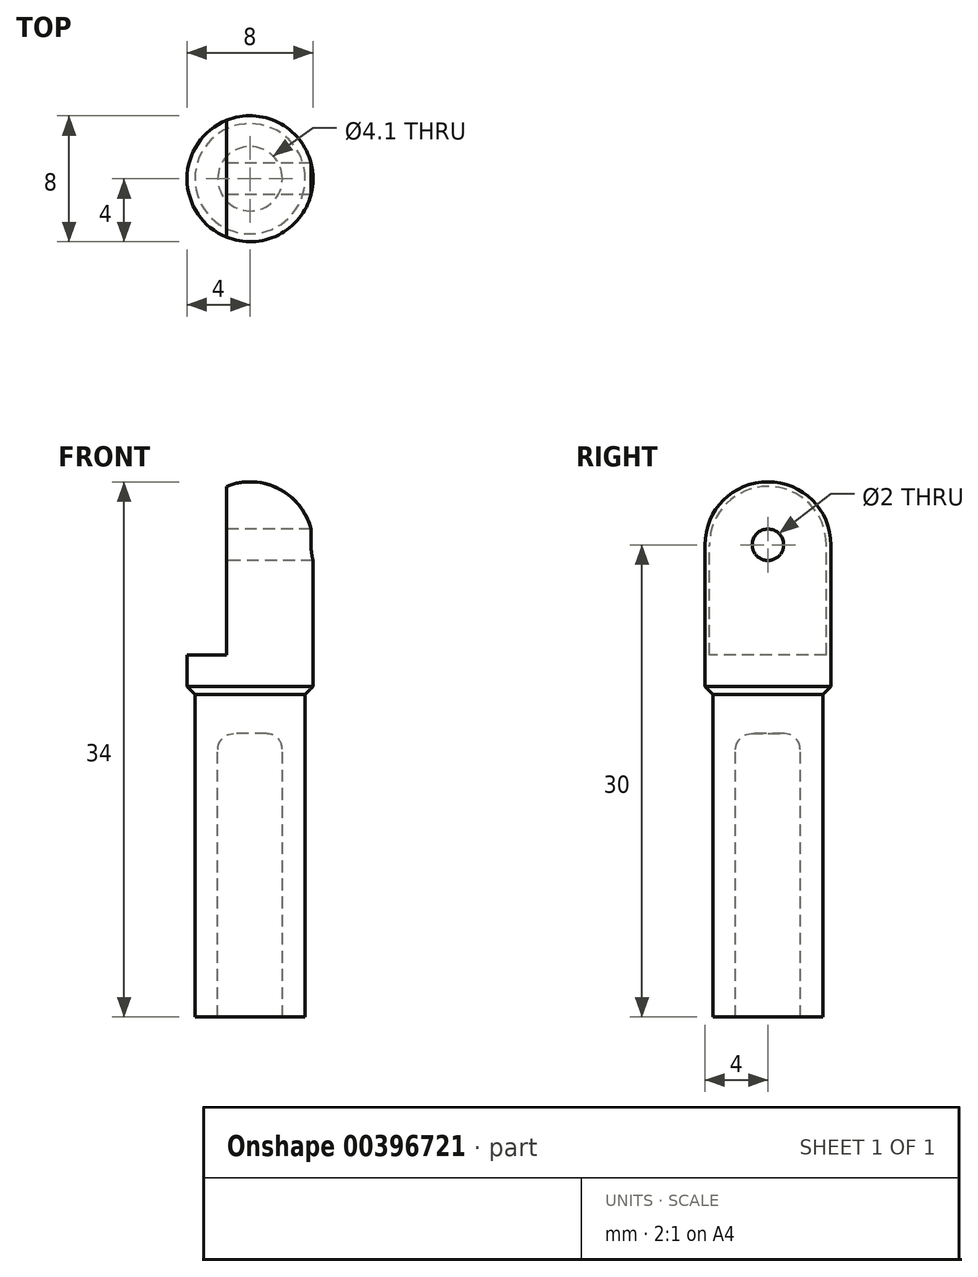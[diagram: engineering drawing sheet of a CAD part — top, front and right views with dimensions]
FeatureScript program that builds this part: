
annotation { "Feature Type Name" : "Feature", "Feature Type Description" : "" }
export const myFeature = defineFeature(function(context is Context, id is Id, definition is map)
    precondition{}
    {
        {
            var Q0;
            Q0=qCreatedBy(makeId("Front.planeOp"),FACE);
            var sketch = newSketch(context, id + "F0", { "sketchPlane" : qUnion([Q0])});
            skLineSegment(sketch, "E0", {"start": v(0, 16) * mm, "end": v(0, 0) * mm, "construction": true});
            skLineSegment(sketch, "E1", {"start": v(2.05, -18) * mm, "end": v(3.5, -18) * mm});
            skLineSegment(sketch, "E2", {"start": v(3.5, -18) * mm, "end": v(3.5, 2.5) * mm});
            skLineSegment(sketch, "E3", {"start": v(4, 3) * mm, "end": v(4, 12) * mm});
            skArc(sketch, "E4", {"start": v(4, 12) * mm, "mid": v(2.83, 14.83) * mm, "end": v(0, 16) * mm});
            skLineSegment(sketch, "E5", {"start": v(0, 16) * mm, "end": v(0, 12) * mm});
            skLineSegment(sketch, "E6", {"start": v(2.05, -18) * mm, "end": v(2.05, -1) * mm});
            skLineSegment(sketch, "E7", {"start": v(1.05, 0) * mm, "end": v(0, 0) * mm});
            skLineSegment(sketch, "E8", {"start": v(0, 12) * mm, "end": v(0, 0) * mm});
            skPoint(sketch, "E9.visualSharp", {"position": v(2.05, 0) * mm});
            skArc(sketch, "E9.filletArc", {"start": v(2.05, -1) * mm, "mid": v(1.76, -0.3) * mm, "end": v(1.05, 0) * mm});
            skLineSegment(sketch, "E10", {"start": v(3.5, 2.5) * mm, "end": v(4, 3) * mm});
            skSolve(sketch);
        }
        {
            var Q0;
            Q0=makeQuery(id+"F0.imprint","IMPRINT",FACE,{"disambiguationData":[TD([[makeQuery(id+"F0.imprint","IMPRINT",EDGE,{"derivedFrom":sQuery(id+"F0.wireOp",EDGE,"E1")}),1.0]])]});
            var Q1;
            Q1=sQuery(id+"F0.wireOp",EDGE,"E5");
            revolve(context, id + "F1", {"entities" : qUnion([Q0]), "axis" : qUnion([Q1]), "revolveType" : RevolveType.FULL});
        }
        {
            var Q0;
            Q0=qCreatedBy(makeId("Front.planeOp"),FACE);
            var sketch = newSketch(context, id + "F2", { "sketchPlane" : qUnion([Q0])});
            skLineSegment(sketch, "E11.bottom", {"start": v(-1.5, 68.3) * mm, "end": v(-82.17, 68.3) * mm});
            skLineSegment(sketch, "E11.top", {"start": v(-1.5, 5) * mm, "end": v(-82.17, 5) * mm});
            skLineSegment(sketch, "E11.left", {"start": v(-1.5, 68.3) * mm, "end": v(-1.5, 5) * mm});
            skLineSegment(sketch, "E11.right", {"start": v(-82.17, 68.3) * mm, "end": v(-82.17, 5) * mm});
            skSolve(sketch);
        }
        {
            var Q0;
            Q0 = qSketchRegion(id + "F2", true);
            extrude(context, id + "F3", {"entities" : qUnion([Q0]), "operationType" : NewBodyOperationType.REMOVE, "endBound" : BoundingType.SYMMETRIC, "oppositeDirection" : true, "depth" : 200 * mm});
        }
        {
            var Q0;
            Q0=makeQuery(id+"F3.boolean.opBoolean","COPY",FACE,{"derivedFrom":makeQuery(id+"F3.opExtrude","SWEPT_FACE",FACE,{"disambiguationData":[OSD([sQuery(id+"F2.wireOp",EDGE,"E11.left")])]})});
            var sketch = newSketch(context, id + "F4", { "sketchPlane" : qUnion([Q0])});
            skCircle(sketch, "E12", {"center": v(0, 12) * mm, "radius": 1 * mm});
            skSolve(sketch);
        }
        {
            var Q0;
            Q0 = qSketchRegion(id + "F4", true);
            extrude(context, id + "F5", {"entities" : qUnion([Q0]), "operationType" : NewBodyOperationType.REMOVE, "endBound" : BoundingType.THROUGH_ALL, "oppositeDirection" : true, "depth" : 25 * mm});
        }
    });
